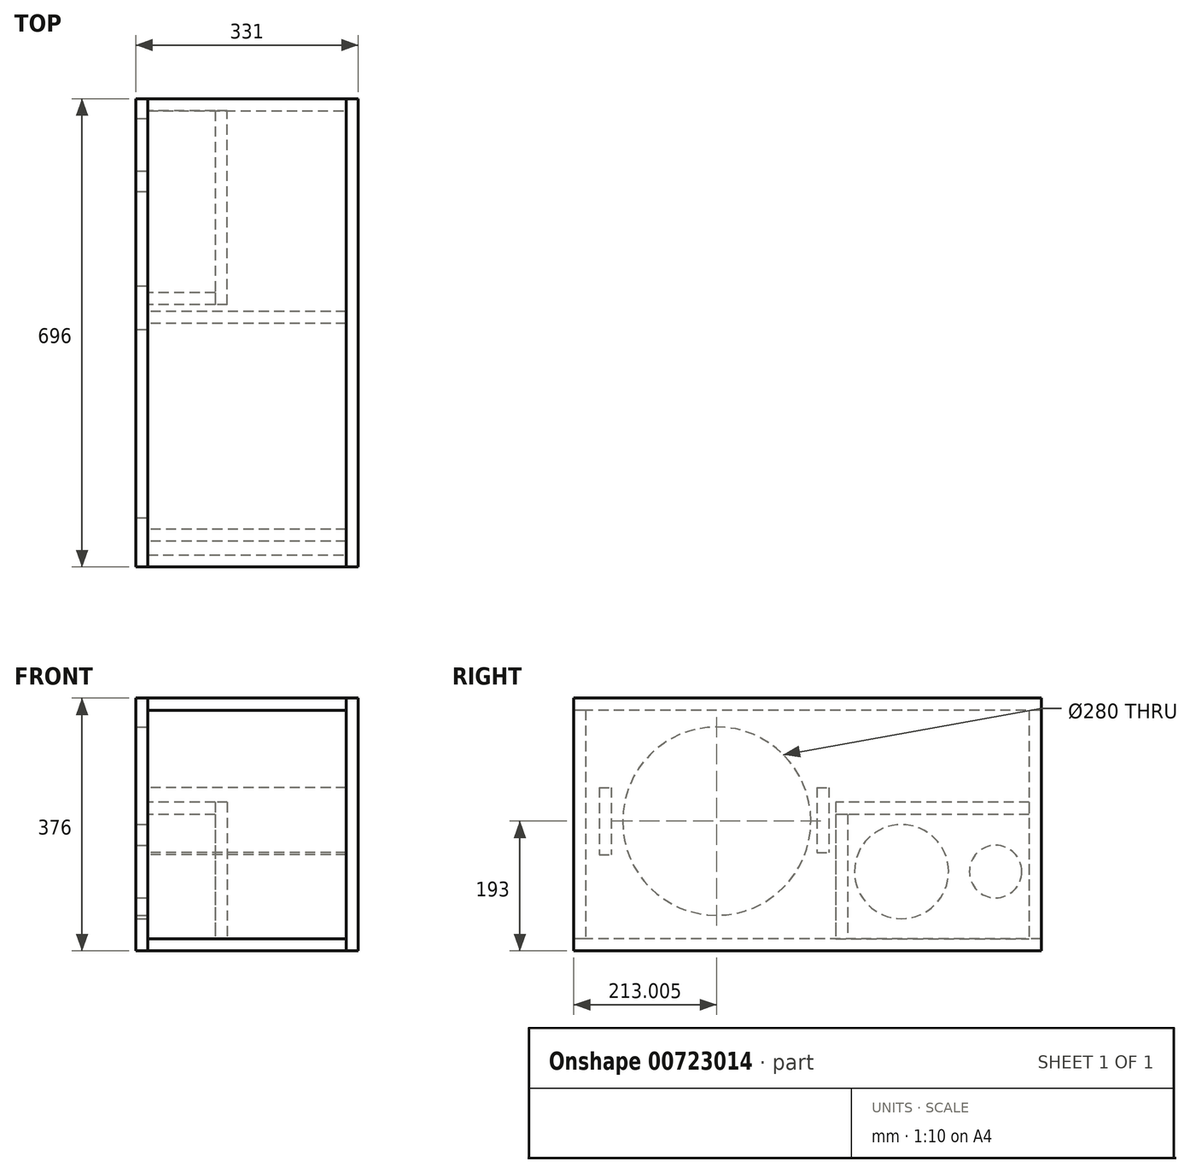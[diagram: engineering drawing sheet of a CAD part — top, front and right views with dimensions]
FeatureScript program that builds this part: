
annotation { "Feature Type Name" : "Feature", "Feature Type Description" : "" }
export const myFeature = defineFeature(function(context is Context, id is Id, definition is map)
    precondition{}
    {
        {
            var Q0;
            Q0=qCreatedBy(makeId("Top.planeOp"),FACE);
            var sketch = newSketch(context, id + "F0", { "sketchPlane" : qUnion([Q0])});
            skLineSegment(sketch, "E0.bottom", {"start": v(-319.6, 355.54) * mm, "end": v(-24.6, 355.54) * mm});
            skLineSegment(sketch, "E0.top", {"start": v(-319.6, -340.46) * mm, "end": v(-24.6, -340.46) * mm});
            skLineSegment(sketch, "E0.left", {"start": v(-319.6, 355.54) * mm, "end": v(-319.6, -340.46) * mm});
            skLineSegment(sketch, "E0.right", {"start": v(-24.6, 355.54) * mm, "end": v(-24.6, -340.46) * mm});
            skSolve(sketch);
        }
        {
            var Q0;
            Q0 = qSketchRegion(id + "F0", true);
            extrude(context, id + "F1", {"entities" : qUnion([Q0]), "depth" : 18 * mm, "offsetDistance" : 25 * mm});
        }
        {
            var Q0;
            Q0=makeQuery(id+"F1.opExtrude","CAP_FACE",FACE,{"disambiguationData":[OSD([sQuery(id+"F0.wireOp",EDGE,"E0.bottom"),sQuery(id+"F0.wireOp",EDGE,"E0.top"),sQuery(id+"F0.wireOp",EDGE,"E0.left"),sQuery(id+"F0.wireOp",EDGE,"E0.right")])],"isStart":false});
            var sketch = newSketch(context, id + "F2", { "sketchPlane" : qUnion([Q0])});
            skLineSegment(sketch, "E1.bottom", {"start": v(-319.6, 355.54) * mm, "end": v(-24.6, 355.54) * mm});
            skLineSegment(sketch, "E1.top", {"start": v(-319.6, 337.54) * mm, "end": v(-24.6, 337.54) * mm});
            skLineSegment(sketch, "E1.left", {"start": v(-319.6, 355.54) * mm, "end": v(-319.6, 337.54) * mm});
            skLineSegment(sketch, "E1.right", {"start": v(-24.6, 355.54) * mm, "end": v(-24.6, 337.54) * mm});
            skLineSegment(sketch, "E2.bottom", {"start": v(-319.6, -340.46) * mm, "end": v(-24.6, -340.46) * mm});
            skLineSegment(sketch, "E2.top", {"start": v(-319.6, -322.46) * mm, "end": v(-24.6, -322.46) * mm});
            skLineSegment(sketch, "E2.left", {"start": v(-319.6, -340.46) * mm, "end": v(-319.6, -322.46) * mm});
            skLineSegment(sketch, "E2.right", {"start": v(-24.6, -340.46) * mm, "end": v(-24.6, -322.46) * mm});
            skSolve(sketch);
        }
        {
            var Q0;
            Q0=makeQuery(id+"F2.imprint","IMPRINT",FACE,{"disambiguationData":[TD([[makeQuery(id+"F2.imprint","IMPRINT",EDGE,{"derivedFrom":sQuery(id+"F2.wireOp",EDGE,"E2.bottom")}),1.0]])]});
            var Q1;
            Q1=makeQuery(id+"F2.imprint","IMPRINT",FACE,{"disambiguationData":[TD([[makeQuery(id+"F2.imprint","IMPRINT",EDGE,{"derivedFrom":sQuery(id+"F2.wireOp",EDGE,"E1.bottom")}),-1.0]])]});
            extrude(context, id + "F3", {"entities" : qUnion([Q0, Q1]), "depth" : 340 * mm, "offsetDistance" : 25 * mm});
        }
        {
            var Q0;
            Q0=makeQuery(id+"F3.opExtrude","SWEPT_FACE",FACE,{"disambiguationData":[OSD([sQuery(id+"F2.wireOp",EDGE,"E1.left")])]});
            var sketch = newSketch(context, id + "F4", { "sketchPlane" : qUnion([Q0])});
            skLineSegment(sketch, "E3.bottom", {"start": v(-337.54, 221) * mm, "end": v(-49.54, 221) * mm});
            skLineSegment(sketch, "E3.top", {"start": v(-337.54, 203) * mm, "end": v(-49.54, 203) * mm});
            skLineSegment(sketch, "E3.left", {"start": v(-337.54, 221) * mm, "end": v(-337.54, 203) * mm});
            skLineSegment(sketch, "E3.right", {"start": v(-49.54, 221) * mm, "end": v(-49.54, 203) * mm});
            skSolve(sketch);
        }
        {
            var Q0;
            Q0 = qSketchRegion(id + "F4", true);
            var Q1;
            Q1=makeQuery(id+"F3.opExtrude","SWEPT_FACE",FACE,{"disambiguationData":[OSD([sQuery(id+"F2.wireOp",EDGE,"E1.right")])]});
            extrude(context, id + "F5", {"entities" : qUnion([Q0]), "oppositeDirection" : true, "depth" : 100 * mm, "endBoundEntityFace" : qUnion([Q1]), "offsetDistance" : 25 * mm});
        }
        {
            var Q0;
            Q0=makeQuery(id+"F5.opExtrude","CAP_FACE",FACE,{"disambiguationData":[OSD([sQuery(id+"F4.wireOp",EDGE,"E3.bottom"),sQuery(id+"F4.wireOp",EDGE,"E3.top"),sQuery(id+"F4.wireOp",EDGE,"E3.left"),sQuery(id+"F4.wireOp",EDGE,"E3.right")])],"isStart":true});
            var sketch = newSketch(context, id + "F6", { "sketchPlane" : qUnion([Q0])});
            skLineSegment(sketch, "E4.bottom", {"start": v(-49.54, 203) * mm, "end": v(-67.54, 203) * mm});
            skLineSegment(sketch, "E4.top", {"start": v(-49.54, 18) * mm, "end": v(-67.54, 18) * mm});
            skLineSegment(sketch, "E4.left", {"start": v(-49.54, 203) * mm, "end": v(-49.54, 18) * mm});
            skLineSegment(sketch, "E4.right", {"start": v(-67.54, 203) * mm, "end": v(-67.54, 18) * mm});
            skSolve(sketch);
        }
        {
            var Q0;
            Q0=makeQuery(id+"F6.imprint","IMPRINT",FACE,{"disambiguationData":[TD([[makeQuery(id+"F6.imprint","IMPRINT",EDGE,{"derivedFrom":sQuery(id+"F6.wireOp",EDGE,"E4.bottom")}),-1.0]])]});
            var Q1;
            Q1=makeQuery(id+"F3.opExtrude","SWEPT_FACE",FACE,{"disambiguationData":[OSD([sQuery(id+"F2.wireOp",EDGE,"E1.right")])]});
            extrude(context, id + "F7", {"entities" : qUnion([Q0]), "oppositeDirection" : true, "depth" : 100 * mm, "endBoundEntityFace" : qUnion([Q1]), "offsetDistance" : 25 * mm});
        }
        {
            var Q0;
            Q0=makeQuery(id+"F1.opExtrude","SWEPT_FACE",FACE,{"disambiguationData":[OSD([sQuery(id+"F0.wireOp",EDGE,"E0.right")])]});
            var sketch = newSketch(context, id + "F8", { "sketchPlane" : qUnion([Q0])});
            skLineSegment(sketch, "E5.bottom", {"start": v(-340.46, 0) * mm, "end": v(355.54, 0) * mm});
            skLineSegment(sketch, "E5.top", {"start": v(-340.46, 376) * mm, "end": v(355.54, 376) * mm});
            skLineSegment(sketch, "E5.left", {"start": v(-340.46, 0) * mm, "end": v(-340.46, 376) * mm});
            skLineSegment(sketch, "E5.right", {"start": v(355.54, 0) * mm, "end": v(355.54, 376) * mm});
            skSolve(sketch);
        }
        {
            var Q0;
            Q0 = qSketchRegion(id + "F8", true);
            extrude(context, id + "F9", {"entities" : qUnion([Q0]), "depth" : 18 * mm, "offsetDistance" : 25 * mm});
        }
        {
            var Q0;
            Q0=makeQuery(id+"F3.opExtrude","CAP_FACE",FACE,{"disambiguationData":[OSD([sQuery(id+"F2.wireOp",EDGE,"E1.bottom"),sQuery(id+"F2.wireOp",EDGE,"E1.top"),sQuery(id+"F2.wireOp",EDGE,"E1.left"),sQuery(id+"F2.wireOp",EDGE,"E1.right")])],"isStart":false});
            var sketch = newSketch(context, id + "F10", { "sketchPlane" : qUnion([Q0])});
            skLineSegment(sketch, "E6.bottom", {"start": v(-24.6, 355.54) * mm, "end": v(-319.6, 355.54) * mm});
            skLineSegment(sketch, "E6.top", {"start": v(-24.6, -340.46) * mm, "end": v(-319.6, -340.46) * mm});
            skLineSegment(sketch, "E6.left", {"start": v(-24.6, 355.54) * mm, "end": v(-24.6, -340.46) * mm});
            skLineSegment(sketch, "E6.right", {"start": v(-319.6, 355.54) * mm, "end": v(-319.6, -340.46) * mm});
            skSolve(sketch);
        }
        {
            var Q0;
            Q0 = qSketchRegion(id + "F10", true);
            extrude(context, id + "F11", {"entities" : qUnion([Q0]), "depth" : 18 * mm, "offsetDistance" : 25 * mm});
        }
        {
            var Q0;
            Q0=makeQuery(id+"F1.opExtrude","SWEPT_FACE",FACE,{"disambiguationData":[OSD([sQuery(id+"F0.wireOp",EDGE,"E0.left")])]});
            var sketch = newSketch(context, id + "F12", { "sketchPlane" : qUnion([Q0])});
            skLineSegment(sketch, "E7.bottom", {"start": v(-355.54, 0) * mm, "end": v(340.46, 0) * mm});
            skLineSegment(sketch, "E7.top", {"start": v(-355.54, 376) * mm, "end": v(340.46, 376) * mm});
            skLineSegment(sketch, "E7.left", {"start": v(-355.54, 0) * mm, "end": v(-355.54, 376) * mm});
            skLineSegment(sketch, "E7.right", {"start": v(340.46, 0) * mm, "end": v(340.46, 376) * mm});
            skCircle(sketch, "E8", {"center": v(-147.54, 118) * mm, "radius": 70 * mm});
            skCircle(sketch, "E9", {"center": v(-287.54, 118) * mm, "radius": 39 * mm});
            skCircle(sketch, "E10", {"center": v(127.46, 193) * mm, "radius": 140 * mm});
            skSolve(sketch);
        }
        {
            var Q0;
            Q0 = qSketchRegion(id + "F12", true);
            extrude(context, id + "F13", {"entities" : qUnion([Q0]), "depth" : 18 * mm, "offsetDistance" : 25 * mm});
        }
        {
            var Q0;
            Q0=makeQuery(id+"F13.opExtrude","CAP_FACE",FACE,{"disambiguationData":[OSD([sQuery(id+"F12.wireOp",EDGE,"E7.bottom"),sQuery(id+"F12.wireOp",EDGE,"E7.top"),sQuery(id+"F12.wireOp",EDGE,"E7.left"),sQuery(id+"F12.wireOp",EDGE,"E7.right"),sQuery(id+"F12.wireOp",EDGE,"E8"),sQuery(id+"F12.wireOp",EDGE,"E9"),sQuery(id+"F12.wireOp",EDGE,"E10")])],"isStart":true});
            var sketch = newSketch(context, id + "F14", { "sketchPlane" : qUnion([Q0])});
            skLineSegment(sketch, "E11.bottom", {"start": v(-302.46, 243) * mm, "end": v(-284.46, 243) * mm});
            skLineSegment(sketch, "E11.top", {"start": v(-302.46, 143) * mm, "end": v(-284.46, 143) * mm});
            skLineSegment(sketch, "E11.left", {"start": v(-302.46, 243) * mm, "end": v(-302.46, 143) * mm});
            skLineSegment(sketch, "E11.right", {"start": v(-284.46, 243) * mm, "end": v(-284.46, 143) * mm});
            skLineSegment(sketch, "E12.bottom", {"start": v(21.54, 243) * mm, "end": v(39.54, 243) * mm});
            skLineSegment(sketch, "E12.top", {"start": v(21.54, 146.4) * mm, "end": v(39.54, 146.4) * mm});
            skLineSegment(sketch, "E12.left", {"start": v(21.54, 243) * mm, "end": v(21.54, 146.4) * mm});
            skLineSegment(sketch, "E12.right", {"start": v(39.54, 243) * mm, "end": v(39.54, 146.4) * mm});
            skSolve(sketch);
        }
        {
            var Q0;
            Q0 = qSketchRegion(id + "F14", true);
            var Q1;
            Q1=makeQuery(id+"F3.opExtrude","SWEPT_FACE",FACE,{"disambiguationData":[OSD([sQuery(id+"F2.wireOp",EDGE,"E2.right")])]});
            extrude(context, id + "F15", {"entities" : qUnion([Q0]), "endBound" : BoundingType.UP_TO_SURFACE, "depth" : 25 * mm, "endBoundEntityFace" : qUnion([Q1]), "offsetDistance" : 25 * mm});
        }
        {
            var Q0;
            Q0=makeQuery(id+"F7.opExtrude","CAP_FACE",FACE,{"disambiguationData":[OSD([sQuery(id+"F6.wireOp",EDGE,"E4.bottom"),sQuery(id+"F6.wireOp",EDGE,"E4.top"),sQuery(id+"F6.wireOp",EDGE,"E4.left"),sQuery(id+"F6.wireOp",EDGE,"E4.right")])],"isStart":false});
            var sketch = newSketch(context, id + "F16", { "sketchPlane" : qUnion([Q0])});
            skLineSegment(sketch, "E13.bottom", {"start": v(49.54, 221) * mm, "end": v(337.54, 221) * mm});
            skLineSegment(sketch, "E13.top", {"start": v(49.54, 18) * mm, "end": v(337.54, 18) * mm});
            skLineSegment(sketch, "E13.left", {"start": v(49.54, 221) * mm, "end": v(49.54, 18) * mm});
            skLineSegment(sketch, "E13.right", {"start": v(337.54, 221) * mm, "end": v(337.54, 18) * mm});
            skSolve(sketch);
        }
        {
            var Q0;
            Q0 = qSketchRegion(id + "F16", true);
            extrude(context, id + "F17", {"entities" : qUnion([Q0]), "depth" : 18 * mm, "offsetDistance" : 25 * mm});
        }
    });
